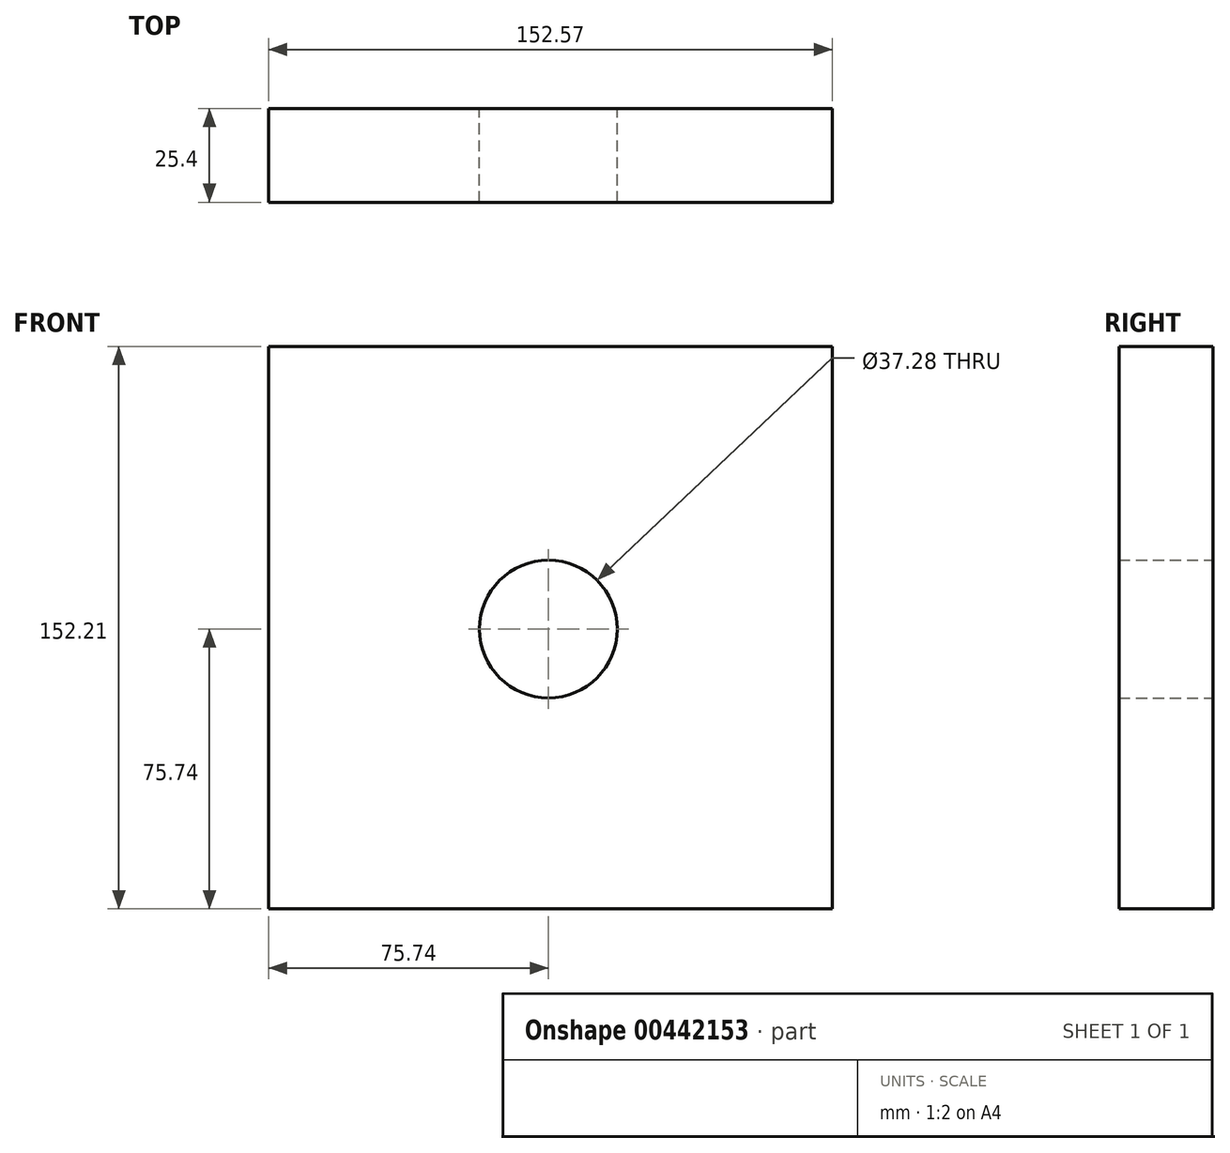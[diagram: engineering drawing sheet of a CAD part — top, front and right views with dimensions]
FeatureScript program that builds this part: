
annotation { "Feature Type Name" : "Feature", "Feature Type Description" : "" }
export const myFeature = defineFeature(function(context is Context, id is Id, definition is map)
    precondition{}
    {
        {
            var Q0;
            Q0=qCreatedBy(makeId("Front.planeOp"),FACE);
            var sketch = newSketch(context, id + "F0", { "sketchPlane" : qUnion([Q0])});
            skCircle(sketch, "E0", {"center": v(0, 0) * mm, "radius": 18.64 * mm});
            skLineSegment(sketch, "E1.bottom", {"start": v(-75.74, 76.47) * mm, "end": v(76.83, 76.47) * mm});
            skLineSegment(sketch, "E1.top", {"start": v(-75.74, -75.74) * mm, "end": v(76.83, -75.74) * mm});
            skLineSegment(sketch, "E1.left", {"start": v(-75.74, 76.47) * mm, "end": v(-75.74, -75.74) * mm});
            skLineSegment(sketch, "E1.right", {"start": v(76.83, 76.47) * mm, "end": v(76.83, -75.74) * mm});
            skSolve(sketch);
        }
        {
            var Q0;
            Q0 = qSketchRegion(id + "F0", true);
            extrude(context, id + "F1", {"entities" : qUnion([Q0]), "depth" : 25.4 * mm});
        }
    });
